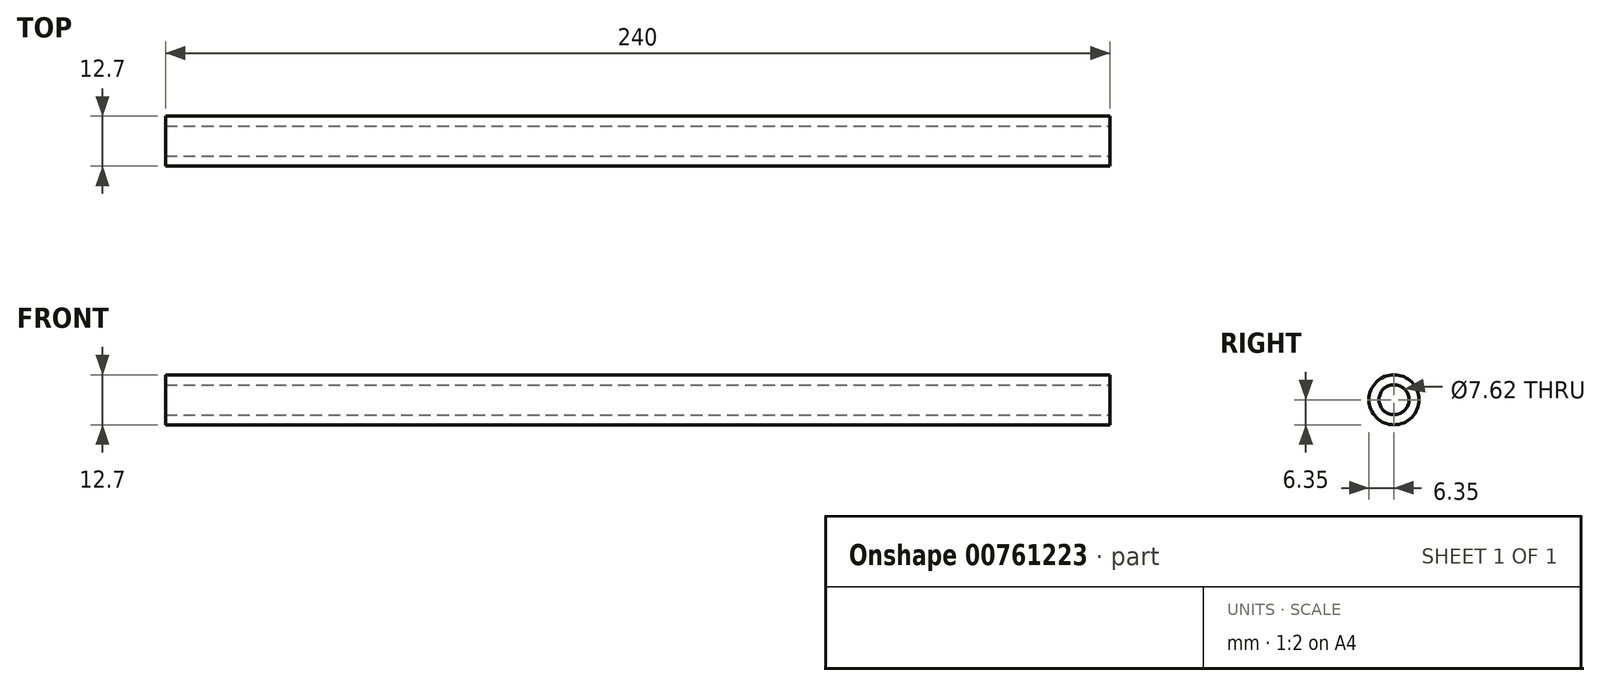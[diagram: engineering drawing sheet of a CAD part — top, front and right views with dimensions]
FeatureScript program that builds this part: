
annotation { "Feature Type Name" : "Feature", "Feature Type Description" : "" }
export const myFeature = defineFeature(function(context is Context, id is Id, definition is map)
    precondition{}
    {
        {
            var Q0;
            Q0=qCreatedBy(makeId("Front.planeOp"),FACE);
            var sketch = newSketch(context, id + "F0", { "sketchPlane" : qUnion([Q0])});
            skLineSegment(sketch, "E0", {"start": v(0, 3.8) * mm, "end": v(-240, 3.8) * mm});
            skLineSegment(sketch, "E1", {"start": v(-240, 3.8) * mm, "end": v(-240, 6.35) * mm});
            skLineSegment(sketch, "E2", {"start": v(-240, 6.35) * mm, "end": v(0, 6.35) * mm});
            skLineSegment(sketch, "E3", {"start": v(0, 6.35) * mm, "end": v(0, 3.8) * mm});
            skLineSegment(sketch, "E4", {"start": v(0, 0) * mm, "end": v(-240, 0) * mm, "construction": true});
            skSolve(sketch);
        }
        {
            var Q0;
            Q0=makeQuery(id+"F0.imprint","IMPRINT",FACE,{"disambiguationData":[TD([[makeQuery(id+"F0.imprint","IMPRINT",EDGE,{"derivedFrom":sQuery(id+"F0.wireOp",EDGE,"E0")}),-1.0]])]});
            var Q1;
            Q1=sQuery(id+"F0.wireOp",EDGE,"E1");
            var Q2;
            Q2=sQuery(id+"F0.wireOp",EDGE,"E2");
            var Q3;
            Q3=sQuery(id+"F0.wireOp",EDGE,"E3");
            var Q4;
            Q4=sQuery(id+"F0.wireOp",EDGE,"E0");
            var Q5;
            Q5=sQuery(id+"F0.wireOp",EDGE,"E4");
            revolve(context, id + "F1", {"surfaceOperationType" : NewSurfaceOperationType.NEW, "entities" : qUnion([Q0]), "surfaceEntities" : qUnion([Q1, Q2, Q3, Q4]), "axis" : qUnion([Q5]), "revolveType" : RevolveType.FULL});
        }
    });
